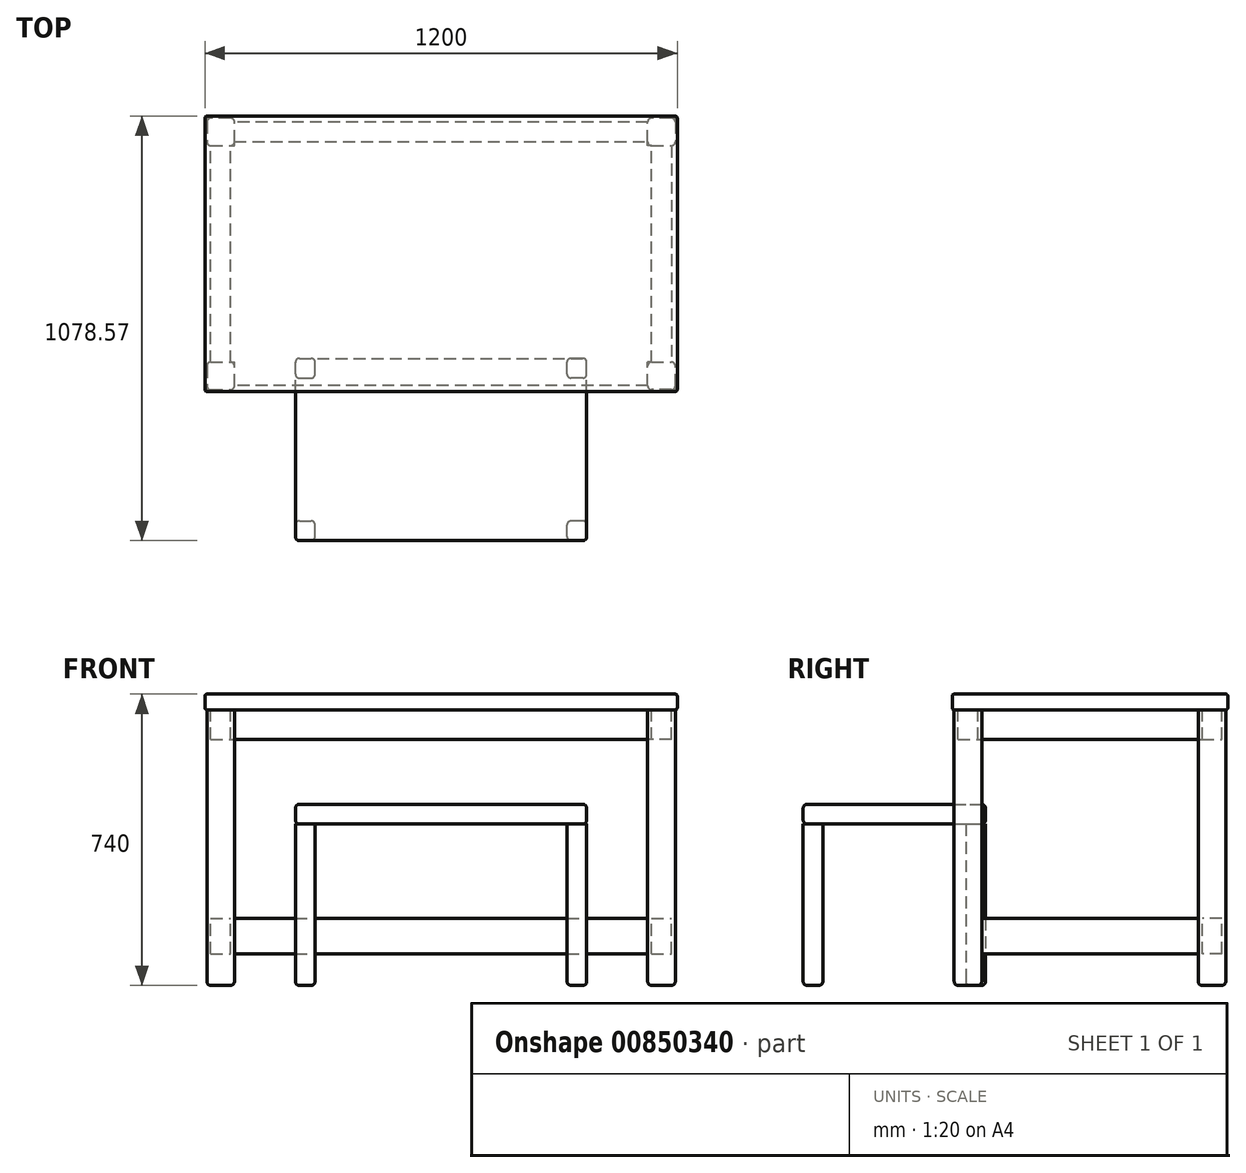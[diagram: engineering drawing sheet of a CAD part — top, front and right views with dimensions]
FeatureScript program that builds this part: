
annotation { "Feature Type Name" : "Feature", "Feature Type Description" : "" }
export const myFeature = defineFeature(function(context is Context, id is Id, definition is map)
    precondition{}
    {
        {
            var Q0;
            Q0=qCreatedBy(makeId("Top.planeOp"),FACE);
            var sketch = newSketch(context, id + "F0", { "sketchPlane" : qUnion([Q0])});
            skLineSegment(sketch, "E0.bottom", {"start": v(60, 35) * mm, "end": v(-60, 35) * mm});
            skLineSegment(sketch, "E0.top", {"start": v(60, -35) * mm, "end": v(-60, -35) * mm});
            skLineSegment(sketch, "E0.left", {"start": v(60, 35) * mm, "end": v(60, -35) * mm});
            skLineSegment(sketch, "E0.right", {"start": v(-60, 35) * mm, "end": v(-60, -35) * mm});
            skPoint(sketch, "E0.middle", {"position": v(0, 0) * mm});
            skSolve(sketch);
        }
        {
            var Q0;
            Q0=qSketchRegion(id+"F0",true);
            extrude(context, id + "F1", {"entities" : qUnion([Q0]), "depth" : 4 * mm, "offsetDistance" : 25 * mm});
        }
        {
            var Q0;
            Q0=makeQuery(id+"F1.opExtrude","CAP_EDGE",EDGE,{"disambiguationData":[OSD([sQuery(id+"F0.wireOp",EDGE,"E0.right")])],"isStart":false});
            var Q1;
            Q1=makeQuery(id+"F1.opExtrude","CAP_EDGE",EDGE,{"disambiguationData":[OSD([sQuery(id+"F0.wireOp",EDGE,"E0.right")])],"isStart":true});
            var Q2;
            Q2=makeQuery(id+"F1.opExtrude","SWEPT_EDGE",EDGE,{"disambiguationData":[OSD([sQuery(id+"F0.wireOp",EDGE,"E0.top"),sQuery(id+"F0.wireOp",EDGE,"E0.right")])]});
            var Q3;
            Q3=makeQuery(id+"F1.opExtrude","CAP_EDGE",EDGE,{"disambiguationData":[OSD([sQuery(id+"F0.wireOp",EDGE,"E0.top")])],"isStart":true});
            var Q4;
            Q4=makeQuery(id+"F1.opExtrude","CAP_EDGE",EDGE,{"disambiguationData":[OSD([sQuery(id+"F0.wireOp",EDGE,"E0.top")])],"isStart":false});
            var Q5;
            Q5=makeQuery(id+"F1.opExtrude","SWEPT_EDGE",EDGE,{"disambiguationData":[OSD([sQuery(id+"F0.wireOp",EDGE,"E0.top"),sQuery(id+"F0.wireOp",EDGE,"E0.left")])]});
            var Q6;
            Q6=makeQuery(id+"F1.opExtrude","CAP_EDGE",EDGE,{"disambiguationData":[OSD([sQuery(id+"F0.wireOp",EDGE,"E0.left")])],"isStart":true});
            var Q7;
            Q7=makeQuery(id+"F1.opExtrude","CAP_EDGE",EDGE,{"disambiguationData":[OSD([sQuery(id+"F0.wireOp",EDGE,"E0.left")])],"isStart":false});
            var Q8;
            Q8=makeQuery(id+"F1.opExtrude","SWEPT_EDGE",EDGE,{"disambiguationData":[OSD([sQuery(id+"F0.wireOp",EDGE,"E0.bottom"),sQuery(id+"F0.wireOp",EDGE,"E0.left")])]});
            var Q9;
            Q9=makeQuery(id+"F1.opExtrude","CAP_EDGE",EDGE,{"disambiguationData":[OSD([sQuery(id+"F0.wireOp",EDGE,"E0.bottom")])],"isStart":false});
            var Q10;
            Q10=makeQuery(id+"F1.opExtrude","CAP_EDGE",EDGE,{"disambiguationData":[OSD([sQuery(id+"F0.wireOp",EDGE,"E0.bottom")])],"isStart":true});
            var Q11;
            Q11=makeQuery(id+"F1.opExtrude","SWEPT_EDGE",EDGE,{"disambiguationData":[OSD([sQuery(id+"F0.wireOp",EDGE,"E0.bottom"),sQuery(id+"F0.wireOp",EDGE,"E0.right")])]});
            fillet(context, id + "F2", {"entities" : qUnion([Q0, Q1, Q2, Q3, Q4, Q5, Q6, Q7, Q8, Q9, Q10, Q11]), "radius" : 0.5 * mm, "tangentPropagation" : true, "allowEdgeOverflow" : false});
        }
        {
            var Q0;
            Q0=qCreatedBy(makeId("Top.planeOp"),FACE);
            var sketch = newSketch(context, id + "F3", { "sketchPlane" : qUnion([Q0])});
            skLineSegment(sketch, "E1.bottom", {"start": v(-59.5, -34.5) * mm, "end": v(-52.5, -34.5) * mm});
            skLineSegment(sketch, "E1.top", {"start": v(-59.5, -27.5) * mm, "end": v(-52.5, -27.5) * mm});
            skLineSegment(sketch, "E1.left", {"start": v(-59.5, -34.5) * mm, "end": v(-59.5, -27.5) * mm});
            skLineSegment(sketch, "E1.right", {"start": v(-52.5, -34.5) * mm, "end": v(-52.5, -27.5) * mm});
            skLineSegment(sketch, "E2.bottom", {"start": v(59.5, -34.5) * mm, "end": v(52.5, -34.5) * mm});
            skLineSegment(sketch, "E2.top", {"start": v(59.5, -27.5) * mm, "end": v(52.5, -27.5) * mm});
            skLineSegment(sketch, "E2.left", {"start": v(59.5, -34.5) * mm, "end": v(59.5, -27.5) * mm});
            skLineSegment(sketch, "E2.right", {"start": v(52.5, -34.5) * mm, "end": v(52.5, -27.5) * mm});
            skLineSegment(sketch, "E3.bottom", {"start": v(59.5, 34.5) * mm, "end": v(52.5, 34.5) * mm});
            skLineSegment(sketch, "E3.top", {"start": v(59.5, 27.5) * mm, "end": v(52.5, 27.5) * mm});
            skLineSegment(sketch, "E3.left", {"start": v(59.5, 34.5) * mm, "end": v(59.5, 27.5) * mm});
            skLineSegment(sketch, "E3.right", {"start": v(52.5, 34.5) * mm, "end": v(52.5, 27.5) * mm});
            skLineSegment(sketch, "E4.bottom", {"start": v(-59.5, 34.5) * mm, "end": v(-52.5, 34.5) * mm});
            skLineSegment(sketch, "E4.top", {"start": v(-59.5, 27.5) * mm, "end": v(-52.5, 27.5) * mm});
            skLineSegment(sketch, "E4.left", {"start": v(-59.5, 34.5) * mm, "end": v(-59.5, 27.5) * mm});
            skLineSegment(sketch, "E4.right", {"start": v(-52.5, 34.5) * mm, "end": v(-52.5, 27.5) * mm});
            skSolve(sketch);
        }
        {
            var Q0;
            Q0=qSketchRegion(id+"F3",true);
            extrude(context, id + "F4", {"entities" : qUnion([Q0]), "operationType" : NewBodyOperationType.ADD, "oppositeDirection" : true, "depth" : 70 * mm, "offsetDistance" : 25 * mm});
        }
        {
            var Q0;
            Q0=makeQuery(id+"F4.opExtrude","SWEPT_EDGE",EDGE,{"disambiguationData":[OSD([sQuery(id+"F3.wireOp",EDGE,"E1.bottom"),sQuery(id+"F3.wireOp",EDGE,"E1.left")])]});
            var Q1;
            Q1=makeQuery(id+"F4.opExtrude","SWEPT_EDGE",EDGE,{"disambiguationData":[OSD([sQuery(id+"F3.wireOp",EDGE,"E1.bottom"),sQuery(id+"F3.wireOp",EDGE,"E1.right")])]});
            var Q2;
            Q2=makeQuery(id+"F4.opExtrude","SWEPT_EDGE",EDGE,{"disambiguationData":[OSD([sQuery(id+"F3.wireOp",EDGE,"E1.top"),sQuery(id+"F3.wireOp",EDGE,"E1.left")])]});
            var Q3;
            Q3=makeQuery(id+"F4.opExtrude","SWEPT_EDGE",EDGE,{"disambiguationData":[OSD([sQuery(id+"F3.wireOp",EDGE,"E1.top"),sQuery(id+"F3.wireOp",EDGE,"E1.right")])]});
            var Q4;
            Q4=makeQuery(id+"F4.opExtrude","CAP_EDGE",EDGE,{"disambiguationData":[OSD([sQuery(id+"F3.wireOp",EDGE,"E1.left")])],"isStart":false});
            var Q5;
            Q5=makeQuery(id+"F4.opExtrude","CAP_EDGE",EDGE,{"disambiguationData":[OSD([sQuery(id+"F3.wireOp",EDGE,"E1.top")])],"isStart":false});
            var Q6;
            Q6=makeQuery(id+"F4.opExtrude","CAP_EDGE",EDGE,{"disambiguationData":[OSD([sQuery(id+"F3.wireOp",EDGE,"E1.right")])],"isStart":false});
            var Q7;
            Q7=makeQuery(id+"F4.opExtrude","CAP_EDGE",EDGE,{"disambiguationData":[OSD([sQuery(id+"F3.wireOp",EDGE,"E1.bottom")])],"isStart":false});
            var Q8;
            Q8=makeQuery(id+"F4.opExtrude","SWEPT_EDGE",EDGE,{"disambiguationData":[OSD([sQuery(id+"F3.wireOp",EDGE,"E2.bottom"),sQuery(id+"F3.wireOp",EDGE,"E2.left")])]});
            var Q9;
            Q9=makeQuery(id+"F4.opExtrude","SWEPT_EDGE",EDGE,{"disambiguationData":[OSD([sQuery(id+"F3.wireOp",EDGE,"E2.top"),sQuery(id+"F3.wireOp",EDGE,"E2.left")])]});
            var Q10;
            Q10=makeQuery(id+"F4.opExtrude","SWEPT_EDGE",EDGE,{"disambiguationData":[OSD([sQuery(id+"F3.wireOp",EDGE,"E2.bottom"),sQuery(id+"F3.wireOp",EDGE,"E2.right")])]});
            var Q11;
            Q11=makeQuery(id+"F4.opExtrude","SWEPT_EDGE",EDGE,{"disambiguationData":[OSD([sQuery(id+"F3.wireOp",EDGE,"E2.top"),sQuery(id+"F3.wireOp",EDGE,"E2.right")])]});
            var Q12;
            Q12=makeQuery(id+"F4.opExtrude","CAP_EDGE",EDGE,{"disambiguationData":[OSD([sQuery(id+"F3.wireOp",EDGE,"E2.bottom")])],"isStart":false});
            var Q13;
            Q13=makeQuery(id+"F4.opExtrude","CAP_EDGE",EDGE,{"disambiguationData":[OSD([sQuery(id+"F3.wireOp",EDGE,"E2.left")])],"isStart":false});
            var Q14;
            Q14=makeQuery(id+"F4.opExtrude","CAP_EDGE",EDGE,{"disambiguationData":[OSD([sQuery(id+"F3.wireOp",EDGE,"E2.top")])],"isStart":false});
            var Q15;
            Q15=makeQuery(id+"F4.opExtrude","CAP_EDGE",EDGE,{"disambiguationData":[OSD([sQuery(id+"F3.wireOp",EDGE,"E2.right")])],"isStart":false});
            var Q16;
            Q16=makeQuery(id+"F4.opExtrude","SWEPT_EDGE",EDGE,{"disambiguationData":[OSD([sQuery(id+"F3.wireOp",EDGE,"E3.bottom"),sQuery(id+"F3.wireOp",EDGE,"E3.left")])]});
            var Q17;
            Q17=makeQuery(id+"F4.opExtrude","SWEPT_EDGE",EDGE,{"disambiguationData":[OSD([sQuery(id+"F3.wireOp",EDGE,"E3.top"),sQuery(id+"F3.wireOp",EDGE,"E3.left")])]});
            var Q18;
            Q18=makeQuery(id+"F4.opExtrude","SWEPT_EDGE",EDGE,{"disambiguationData":[OSD([sQuery(id+"F3.wireOp",EDGE,"E3.bottom"),sQuery(id+"F3.wireOp",EDGE,"E3.right")])]});
            var Q19;
            Q19=makeQuery(id+"F4.opExtrude","SWEPT_EDGE",EDGE,{"disambiguationData":[OSD([sQuery(id+"F3.wireOp",EDGE,"E3.top"),sQuery(id+"F3.wireOp",EDGE,"E3.right")])]});
            var Q20;
            Q20=makeQuery(id+"F4.opExtrude","CAP_EDGE",EDGE,{"disambiguationData":[OSD([sQuery(id+"F3.wireOp",EDGE,"E3.top")])],"isStart":false});
            var Q21;
            Q21=makeQuery(id+"F4.opExtrude","CAP_EDGE",EDGE,{"disambiguationData":[OSD([sQuery(id+"F3.wireOp",EDGE,"E3.left")])],"isStart":false});
            var Q22;
            Q22=makeQuery(id+"F4.opExtrude","CAP_EDGE",EDGE,{"disambiguationData":[OSD([sQuery(id+"F3.wireOp",EDGE,"E3.bottom")])],"isStart":false});
            var Q23;
            Q23=makeQuery(id+"F4.opExtrude","CAP_EDGE",EDGE,{"disambiguationData":[OSD([sQuery(id+"F3.wireOp",EDGE,"E3.right")])],"isStart":false});
            var Q24;
            Q24=makeQuery(id+"F4.opExtrude","SWEPT_EDGE",EDGE,{"disambiguationData":[OSD([sQuery(id+"F3.wireOp",EDGE,"E4.top"),sQuery(id+"F3.wireOp",EDGE,"E4.left")])]});
            var Q25;
            Q25=makeQuery(id+"F4.opExtrude","SWEPT_EDGE",EDGE,{"disambiguationData":[OSD([sQuery(id+"F3.wireOp",EDGE,"E4.top"),sQuery(id+"F3.wireOp",EDGE,"E4.right")])]});
            var Q26;
            Q26=makeQuery(id+"F4.opExtrude","SWEPT_EDGE",EDGE,{"disambiguationData":[OSD([sQuery(id+"F3.wireOp",EDGE,"E4.bottom"),sQuery(id+"F3.wireOp",EDGE,"E4.left")])]});
            var Q27;
            Q27=makeQuery(id+"F4.opExtrude","SWEPT_EDGE",EDGE,{"disambiguationData":[OSD([sQuery(id+"F3.wireOp",EDGE,"E4.bottom"),sQuery(id+"F3.wireOp",EDGE,"E4.right")])]});
            var Q28;
            Q28=makeQuery(id+"F4.opExtrude","CAP_EDGE",EDGE,{"disambiguationData":[OSD([sQuery(id+"F3.wireOp",EDGE,"E4.right")])],"isStart":false});
            var Q29;
            Q29=makeQuery(id+"F4.opExtrude","CAP_EDGE",EDGE,{"disambiguationData":[OSD([sQuery(id+"F3.wireOp",EDGE,"E4.top")])],"isStart":false});
            var Q30;
            Q30=makeQuery(id+"F4.opExtrude","CAP_EDGE",EDGE,{"disambiguationData":[OSD([sQuery(id+"F3.wireOp",EDGE,"E4.bottom")])],"isStart":false});
            var Q31;
            Q31=makeQuery(id+"F4.opExtrude","CAP_EDGE",EDGE,{"disambiguationData":[OSD([sQuery(id+"F3.wireOp",EDGE,"E4.left")])],"isStart":false});
            fillet(context, id + "F5", {"entities" : qUnion([Q0, Q1, Q2, Q3, Q4, Q5, Q6, Q7, Q8, Q9, Q10, Q11, Q12, Q13, Q14, Q15, Q16, Q17, Q18, Q19, Q20, Q21, Q22, Q23, Q24, Q25, Q26, Q27, Q28, Q29, Q30, Q31]), "radius" : 1 * mm, "tangentPropagation" : true, "allowEdgeOverflow" : false});
        }
        {
            var Q0;
            Q0=makeQuery(id+"F4.opExtrude","SWEPT_FACE",FACE,{"disambiguationData":[OSD([sQuery(id+"F3.wireOp",EDGE,"E3.top")])]});
            var sketch = newSketch(context, id + "F6", { "sketchPlane" : qUnion([Q0])});
            skLineSegment(sketch, "E5.bottom", {"start": v(53.5, -62) * mm, "end": v(58.5, -62) * mm});
            skLineSegment(sketch, "E5.top", {"start": v(53.5, -53) * mm, "end": v(58.5, -53) * mm});
            skLineSegment(sketch, "E5.left", {"start": v(53.5, -62) * mm, "end": v(53.5, -53) * mm});
            skLineSegment(sketch, "E5.right", {"start": v(58.5, -62) * mm, "end": v(58.5, -53) * mm});
            skSolve(sketch);
        }
        {
            var Q0;
            Q0=qSketchRegion(id+"F6",true);
            extrude(context, id + "F7", {"entities" : qUnion([Q0]), "operationType" : NewBodyOperationType.ADD, "depth" : 55 * mm, "offsetDistance" : 25 * mm});
        }
        {
            var Q0;
            Q0=makeQuery(id+"F4.opExtrude","SWEPT_FACE",FACE,{"disambiguationData":[OSD([sQuery(id+"F3.wireOp",EDGE,"E4.top")])]});
            var sketch = newSketch(context, id + "F8", { "sketchPlane" : qUnion([Q0])});
            skLineSegment(sketch, "E6.bottom", {"start": v(-58.5, -62) * mm, "end": v(-53.5, -62) * mm});
            skLineSegment(sketch, "E6.top", {"start": v(-58.5, -53) * mm, "end": v(-53.5, -53) * mm});
            skLineSegment(sketch, "E6.left", {"start": v(-58.5, -62) * mm, "end": v(-58.5, -53) * mm});
            skLineSegment(sketch, "E6.right", {"start": v(-53.5, -62) * mm, "end": v(-53.5, -53) * mm});
            skSolve(sketch);
        }
        {
            var Q0;
            Q0=qSketchRegion(id+"F8",true);
            extrude(context, id + "F9", {"entities" : qUnion([Q0]), "operationType" : NewBodyOperationType.ADD, "depth" : 55 * mm, "offsetDistance" : 25 * mm});
        }
        {
            var Q0;
            Q0=makeQuery(id+"F4.opExtrude","SWEPT_FACE",FACE,{"disambiguationData":[OSD([sQuery(id+"F3.wireOp",EDGE,"E3.right")])]});
            var sketch = newSketch(context, id + "F10", { "sketchPlane" : qUnion([Q0])});
            skLineSegment(sketch, "E7.bottom", {"start": v(-33.5, -62) * mm, "end": v(-28.5, -62) * mm});
            skLineSegment(sketch, "E7.top", {"start": v(-33.5, -53) * mm, "end": v(-28.5, -53) * mm});
            skLineSegment(sketch, "E7.left", {"start": v(-33.5, -62) * mm, "end": v(-33.5, -53) * mm});
            skLineSegment(sketch, "E7.right", {"start": v(-28.5, -62) * mm, "end": v(-28.5, -53) * mm});
            skSolve(sketch);
        }
        {
            var Q0;
            Q0=qSketchRegion(id+"F10",true);
            extrude(context, id + "F11", {"entities" : qUnion([Q0]), "operationType" : NewBodyOperationType.ADD, "depth" : 105 * mm, "offsetDistance" : 25 * mm});
        }
        {
            var Q0;
            Q0=makeQuery(id+"F4.opExtrude","SWEPT_FACE",FACE,{"disambiguationData":[OSD([sQuery(id+"F3.wireOp",EDGE,"E1.right")])]});
            var sketch = newSketch(context, id + "F12", { "sketchPlane" : qUnion([Q0])});
            skLineSegment(sketch, "E8.bottom", {"start": v(-33.5, -7.5) * mm, "end": v(33.5, -7.5) * mm});
            skLineSegment(sketch, "E8.top", {"start": v(-33.5, 0) * mm, "end": v(33.5, 0) * mm});
            skLineSegment(sketch, "E8.left", {"start": v(-33.5, -7.5) * mm, "end": v(-33.5, 0) * mm});
            skLineSegment(sketch, "E8.right", {"start": v(33.5, -7.5) * mm, "end": v(33.5, 0) * mm});
            skSolve(sketch);
        }
        {
            var Q0;
            Q0=qSketchRegion(id+"F12",true);
            extrude(context, id + "F13", {"entities" : qUnion([Q0]), "operationType" : NewBodyOperationType.ADD, "depth" : 105 * mm, "offsetDistance" : 25 * mm});
        }
        {
            var Q0;
            {var subQ1=sQuery(id+"F3.wireOp",EDGE,"E2.top");Q0=makeQuery(id+"F7.boolean.opBoolean","SPLIT",FACE,{"disambiguationData":[TD([makeQuery(id+"F7.opExtrude","SWEPT_FACE",FACE,{"disambiguationData":[OSD([sQuery(id+"F6.wireOp",EDGE,"E5.top")])]})])],"derivedFrom":makeQuery(id+"F4.opExtrude","SWEPT_FACE",FACE,{"disambiguationData":[OSD([subQ1])]})});}
            var sketch = newSketch(context, id + "F14", { "sketchPlane" : qUnion([Q0])});
            skLineSegment(sketch, "E9.bottom", {"start": v(-58.5, -7.5) * mm, "end": v(-52.5, -7.5) * mm});
            skLineSegment(sketch, "E9.top", {"start": v(-58.5, 0) * mm, "end": v(-52.5, 0) * mm});
            skLineSegment(sketch, "E9.left", {"start": v(-58.5, -7.5) * mm, "end": v(-58.5, 0) * mm});
            skLineSegment(sketch, "E9.right", {"start": v(-52.5, -7.5) * mm, "end": v(-52.5, 0) * mm});
            skSolve(sketch);
        }
        {
            var Q0;
            Q0=qSketchRegion(id+"F14",true);
            extrude(context, id + "F15", {"entities" : qUnion([Q0]), "operationType" : NewBodyOperationType.ADD, "depth" : 55 * mm, "offsetDistance" : 25 * mm});
        }
        {
            var Q0;
            {var subQ1=sQuery(id+"F3.wireOp",EDGE,"E4.top");Q0=makeQuery(id+"F9.boolean.opBoolean","SPLIT",FACE,{"disambiguationData":[TD([makeQuery(id+"F9.opExtrude","SWEPT_FACE",FACE,{"disambiguationData":[OSD([sQuery(id+"F8.wireOp",EDGE,"E6.top")])]})])],"derivedFrom":makeQuery(id+"F4.opExtrude","SWEPT_FACE",FACE,{"disambiguationData":[OSD([subQ1])]})});}
            var sketch = newSketch(context, id + "F16", { "sketchPlane" : qUnion([Q0])});
            skLineSegment(sketch, "E10.bottom", {"start": v(-58.5, -7.5) * mm, "end": v(-52.5, -7.5) * mm});
            skLineSegment(sketch, "E10.top", {"start": v(-58.5, 0) * mm, "end": v(-52.5, 0) * mm});
            skLineSegment(sketch, "E10.left", {"start": v(-58.5, -7.5) * mm, "end": v(-58.5, 0) * mm});
            skLineSegment(sketch, "E10.right", {"start": v(-52.5, -7.5) * mm, "end": v(-52.5, 0) * mm});
            skSolve(sketch);
        }
        {
            var Q0;
            Q0=qSketchRegion(id+"F16",true);
            extrude(context, id + "F17", {"entities" : qUnion([Q0]), "operationType" : NewBodyOperationType.ADD, "depth" : 55 * mm, "offsetDistance" : 25 * mm});
        }
        {
            var Q0;
            Q0=makeQuery(id+"F1.opExtrude","SWEPT_BODY",BODY,{"disambiguationData":[OSD([sQuery(id+"F0.wireOp",EDGE,"E0.bottom"),sQuery(id+"F0.wireOp",EDGE,"E0.top"),sQuery(id+"F0.wireOp",EDGE,"E0.left"),sQuery(id+"F0.wireOp",EDGE,"E0.right")])]});
            var Q1;
            Q1=qCreatedBy(makeId("Origin.pointOp"),VERTEX);
            transform(context, id + "F18", {"entities" : qUnion([Q0]), "transformType" : TransformType.SCALE_UNIFORMLY, "scale" : 10, "scalePoint" : qUnion([Q1]), "makeCopy" : false});
        }
        {
            var Q0;
            Q0=makeQuery(id+"F4.opExtrude","CAP_FACE",FACE,{"disambiguationData":[OSD([sQuery(id+"F3.wireOp",EDGE,"E1.bottom"),sQuery(id+"F3.wireOp",EDGE,"E1.top"),sQuery(id+"F3.wireOp",EDGE,"E1.left"),sQuery(id+"F3.wireOp",EDGE,"E1.right")])],"isStart":false});
            var sketch = newSketch(context, id + "F19", { "sketchPlane" : qUnion([Q0])});
            skLineSegment(sketch, "E11.bottom", {"start": v(-370.07, 315.43) * mm, "end": v(-320.07, 315.43) * mm});
            skLineSegment(sketch, "E11.top", {"start": v(-370.07, 265.43) * mm, "end": v(-320.07, 265.43) * mm});
            skLineSegment(sketch, "E11.left", {"start": v(-370.07, 315.43) * mm, "end": v(-370.07, 265.43) * mm});
            skLineSegment(sketch, "E11.right", {"start": v(-320.07, 315.43) * mm, "end": v(-320.07, 265.43) * mm});
            skSolve(sketch);
        }
        {
            var Q0;
            Q0=qSketchRegion(id+"F19",true);
            extrude(context, id + "F20", {"entities" : qUnion([Q0]), "oppositeDirection" : true, "depth" : 410 * mm, "offsetDistance" : 25 * mm});
        }
        {
            var Q0;
            Q0=makeQuery(id+"F20.opExtrude","SWEPT_BODY",BODY,{"disambiguationData":[OSD([sQuery(id+"F19.wireOp",EDGE,"E11.bottom"),sQuery(id+"F19.wireOp",EDGE,"E11.top"),sQuery(id+"F19.wireOp",EDGE,"E11.left"),sQuery(id+"F19.wireOp",EDGE,"E11.right")])]});
            var Q1;
            Q1=qCreatedBy(makeId("Right.planeOp"),FACE);
            mirror(context, id + "F21", {"entities" : qUnion([Q0]), "mirrorPlane" : qUnion([Q1])});
        }
        {
            var Q0;
            Q0=makeQuery(id+"F20.opExtrude","CAP_FACE",FACE,{"disambiguationData":[OSD([sQuery(id+"F19.wireOp",EDGE,"E11.bottom"),sQuery(id+"F19.wireOp",EDGE,"E11.top"),sQuery(id+"F19.wireOp",EDGE,"E11.left"),sQuery(id+"F19.wireOp",EDGE,"E11.right")])],"isStart":true});
            var sketch = newSketch(context, id + "F22", { "sketchPlane" : qUnion([Q0])});
            skLineSegment(sketch, "E12.bottom", {"start": v(-370.07, 528.57) * mm, "end": v(-320.07, 528.57) * mm});
            skLineSegment(sketch, "E12.top", {"start": v(-370.07, 478.57) * mm, "end": v(-320.07, 478.57) * mm});
            skLineSegment(sketch, "E12.left", {"start": v(-370.07, 528.57) * mm, "end": v(-370.07, 478.57) * mm});
            skLineSegment(sketch, "E12.right", {"start": v(-320.07, 528.57) * mm, "end": v(-320.07, 478.57) * mm});
            skSolve(sketch);
        }
        {
            var Q0;
            Q0=qSketchRegion(id+"F22",true);
            extrude(context, id + "F23", {"entities" : qUnion([Q0]), "oppositeDirection" : true, "depth" : 410 * mm, "offsetDistance" : 25 * mm});
        }
        {
            var Q0;
            Q0=makeQuery(id+"F23.opExtrude","SWEPT_BODY",BODY,{"disambiguationData":[OSD([sQuery(id+"F22.wireOp",EDGE,"E12.bottom"),sQuery(id+"F22.wireOp",EDGE,"E12.top"),sQuery(id+"F22.wireOp",EDGE,"E12.left"),sQuery(id+"F22.wireOp",EDGE,"E12.right")])]});
            transform(context, id + "F24", {"entities" : qUnion([Q0]), "transformType" : TransformType.TRANSLATION_3D, "dx" : 0 * mm, "dy" : -200 * mm, "dz" : 0 * mm, "makeCopy" : false});
        }
        {
            var Q0;
            Q0=makeQuery(id+"F23.opExtrude","SWEPT_BODY",BODY,{"disambiguationData":[OSD([sQuery(id+"F22.wireOp",EDGE,"E12.bottom"),sQuery(id+"F22.wireOp",EDGE,"E12.top"),sQuery(id+"F22.wireOp",EDGE,"E12.left"),sQuery(id+"F22.wireOp",EDGE,"E12.right")])]});
            var Q1;
            Q1=qCreatedBy(makeId("Right.planeOp"),FACE);
            mirror(context, id + "F25", {"entities" : qUnion([Q0]), "mirrorPlane" : qUnion([Q1])});
        }
        {
            var Q0;
            Q0=makeQuery(id+"F23.opExtrude","CAP_FACE",FACE,{"disambiguationData":[OSD([sQuery(id+"F22.wireOp",EDGE,"E12.bottom"),sQuery(id+"F22.wireOp",EDGE,"E12.top"),sQuery(id+"F22.wireOp",EDGE,"E12.left"),sQuery(id+"F22.wireOp",EDGE,"E12.right")])],"isStart":false});
            var sketch = newSketch(context, id + "F26", { "sketchPlane" : qUnion([Q0])});
            skLineSegment(sketch, "E13.bottom", {"start": v(-370.07, -728.57) * mm, "end": v(370.04, -728.57) * mm});
            skLineSegment(sketch, "E13.top", {"start": v(-370.07, -265.45) * mm, "end": v(370.04, -265.45) * mm});
            skLineSegment(sketch, "E13.left", {"start": v(-370.07, -728.57) * mm, "end": v(-370.07, -265.45) * mm});
            skLineSegment(sketch, "E13.right", {"start": v(370.04, -728.57) * mm, "end": v(370.04, -265.45) * mm});
            skSolve(sketch);
        }
        {
            var Q0;
            Q0=qSketchRegion(id+"F26",true);
            extrude(context, id + "F27", {"entities" : qUnion([Q0]), "depth" : 50 * mm, "offsetDistance" : 25 * mm});
        }
        {
            var Q0;
            Q0=makeQuery(id+"F23.opExtrude","SWEPT_EDGE",EDGE,{"disambiguationData":[OSD([sQuery(id+"F22.wireOp",EDGE,"E12.bottom"),sQuery(id+"F22.wireOp",EDGE,"E12.left")])]});
            var Q1;
            Q1=makeQuery(id+"F23.opExtrude","SWEPT_EDGE",EDGE,{"disambiguationData":[OSD([sQuery(id+"F22.wireOp",EDGE,"E12.bottom"),sQuery(id+"F22.wireOp",EDGE,"E12.right")])]});
            var Q2;
            Q2=makeQuery(id+"F23.opExtrude","SWEPT_EDGE",EDGE,{"disambiguationData":[OSD([sQuery(id+"F22.wireOp",EDGE,"E12.top"),sQuery(id+"F22.wireOp",EDGE,"E12.right")])]});
            var Q3;
            Q3=makeQuery(id+"F23.opExtrude","SWEPT_EDGE",EDGE,{"disambiguationData":[OSD([sQuery(id+"F22.wireOp",EDGE,"E12.top"),sQuery(id+"F22.wireOp",EDGE,"E12.left")])]});
            var Q4;
            Q4=makeQuery(id+"F20.opExtrude","SWEPT_EDGE",EDGE,{"disambiguationData":[OSD([sQuery(id+"F19.wireOp",EDGE,"E11.top"),sQuery(id+"F19.wireOp",EDGE,"E11.left")])]});
            var Q5;
            Q5=makeQuery(id+"F20.opExtrude","SWEPT_EDGE",EDGE,{"disambiguationData":[OSD([sQuery(id+"F19.wireOp",EDGE,"E11.top"),sQuery(id+"F19.wireOp",EDGE,"E11.right")])]});
            var Q6;
            Q6=makeQuery(id+"F20.opExtrude","SWEPT_EDGE",EDGE,{"disambiguationData":[OSD([sQuery(id+"F19.wireOp",EDGE,"E11.bottom"),sQuery(id+"F19.wireOp",EDGE,"E11.left")])]});
            var Q7;
            Q7=makeQuery(id+"F20.opExtrude","SWEPT_EDGE",EDGE,{"disambiguationData":[OSD([sQuery(id+"F19.wireOp",EDGE,"E11.bottom"),sQuery(id+"F19.wireOp",EDGE,"E11.right")])]});
            var Q8;
            Q8=makeQuery(id+"F25.opPattern","COPY",EDGE,{"derivedFrom":makeQuery(id+"F23.opExtrude","SWEPT_EDGE",EDGE,{"disambiguationData":[OSD([sQuery(id+"F22.wireOp",EDGE,"E12.bottom"),sQuery(id+"F22.wireOp",EDGE,"E12.left")])]}),"instanceName":"1"});
            var Q9;
            Q9=makeQuery(id+"F25.opPattern","COPY",EDGE,{"derivedFrom":makeQuery(id+"F23.opExtrude","SWEPT_EDGE",EDGE,{"disambiguationData":[OSD([sQuery(id+"F22.wireOp",EDGE,"E12.top"),sQuery(id+"F22.wireOp",EDGE,"E12.left")])]}),"instanceName":"1"});
            var Q10;
            Q10=makeQuery(id+"F25.opPattern","COPY",EDGE,{"derivedFrom":makeQuery(id+"F23.opExtrude","SWEPT_EDGE",EDGE,{"disambiguationData":[OSD([sQuery(id+"F22.wireOp",EDGE,"E12.bottom"),sQuery(id+"F22.wireOp",EDGE,"E12.right")])]}),"instanceName":"1"});
            var Q11;
            Q11=makeQuery(id+"F25.opPattern","COPY",EDGE,{"derivedFrom":makeQuery(id+"F23.opExtrude","SWEPT_EDGE",EDGE,{"disambiguationData":[OSD([sQuery(id+"F22.wireOp",EDGE,"E12.top"),sQuery(id+"F22.wireOp",EDGE,"E12.right")])]}),"instanceName":"1"});
            var Q12;
            Q12=makeQuery(id+"F21.opPattern","COPY",EDGE,{"derivedFrom":makeQuery(id+"F20.opExtrude","SWEPT_EDGE",EDGE,{"disambiguationData":[OSD([sQuery(id+"F19.wireOp",EDGE,"E11.bottom"),sQuery(id+"F19.wireOp",EDGE,"E11.right")])]}),"instanceName":"1"});
            var Q13;
            Q13=makeQuery(id+"F21.opPattern","COPY",EDGE,{"derivedFrom":makeQuery(id+"F20.opExtrude","SWEPT_EDGE",EDGE,{"disambiguationData":[OSD([sQuery(id+"F19.wireOp",EDGE,"E11.bottom"),sQuery(id+"F19.wireOp",EDGE,"E11.left")])]}),"instanceName":"1"});
            var Q14;
            Q14=makeQuery(id+"F21.opPattern","COPY",EDGE,{"derivedFrom":makeQuery(id+"F20.opExtrude","SWEPT_EDGE",EDGE,{"disambiguationData":[OSD([sQuery(id+"F19.wireOp",EDGE,"E11.top"),sQuery(id+"F19.wireOp",EDGE,"E11.right")])]}),"instanceName":"1"});
            var Q15;
            Q15=makeQuery(id+"F21.opPattern","COPY",EDGE,{"derivedFrom":makeQuery(id+"F20.opExtrude","SWEPT_EDGE",EDGE,{"disambiguationData":[OSD([sQuery(id+"F19.wireOp",EDGE,"E11.top"),sQuery(id+"F19.wireOp",EDGE,"E11.left")])]}),"instanceName":"1"});
            var Q16;
            Q16=makeQuery(id+"F21.opPattern","COPY",EDGE,{"derivedFrom":makeQuery(id+"F20.opExtrude","CAP_EDGE",EDGE,{"disambiguationData":[OSD([sQuery(id+"F19.wireOp",EDGE,"E11.left")])],"isStart":true}),"instanceName":"1"});
            var Q17;
            Q17=makeQuery(id+"F21.opPattern","COPY",EDGE,{"derivedFrom":makeQuery(id+"F20.opExtrude","CAP_EDGE",EDGE,{"disambiguationData":[OSD([sQuery(id+"F19.wireOp",EDGE,"E11.top")])],"isStart":true}),"instanceName":"1"});
            var Q18;
            Q18=makeQuery(id+"F21.opPattern","COPY",EDGE,{"derivedFrom":makeQuery(id+"F20.opExtrude","CAP_EDGE",EDGE,{"disambiguationData":[OSD([sQuery(id+"F19.wireOp",EDGE,"E11.right")])],"isStart":true}),"instanceName":"1"});
            var Q19;
            Q19=makeQuery(id+"F21.opPattern","COPY",EDGE,{"derivedFrom":makeQuery(id+"F20.opExtrude","CAP_EDGE",EDGE,{"disambiguationData":[OSD([sQuery(id+"F19.wireOp",EDGE,"E11.bottom")])],"isStart":true}),"instanceName":"1"});
            var Q20;
            Q20=makeQuery(id+"F20.opExtrude","CAP_EDGE",EDGE,{"disambiguationData":[OSD([sQuery(id+"F19.wireOp",EDGE,"E11.right")])],"isStart":true});
            var Q21;
            Q21=makeQuery(id+"F20.opExtrude","CAP_EDGE",EDGE,{"disambiguationData":[OSD([sQuery(id+"F19.wireOp",EDGE,"E11.top")])],"isStart":true});
            var Q22;
            Q22=makeQuery(id+"F20.opExtrude","CAP_EDGE",EDGE,{"disambiguationData":[OSD([sQuery(id+"F19.wireOp",EDGE,"E11.bottom")])],"isStart":true});
            var Q23;
            Q23=makeQuery(id+"F20.opExtrude","CAP_EDGE",EDGE,{"disambiguationData":[OSD([sQuery(id+"F19.wireOp",EDGE,"E11.left")])],"isStart":true});
            var Q24;
            Q24=makeQuery(id+"F23.opExtrude","CAP_EDGE",EDGE,{"disambiguationData":[OSD([sQuery(id+"F22.wireOp",EDGE,"E12.bottom")])],"isStart":true});
            var Q25;
            Q25=makeQuery(id+"F23.opExtrude","CAP_EDGE",EDGE,{"disambiguationData":[OSD([sQuery(id+"F22.wireOp",EDGE,"E12.left")])],"isStart":true});
            var Q26;
            Q26=makeQuery(id+"F23.opExtrude","CAP_EDGE",EDGE,{"disambiguationData":[OSD([sQuery(id+"F22.wireOp",EDGE,"E12.top")])],"isStart":true});
            var Q27;
            Q27=makeQuery(id+"F23.opExtrude","CAP_EDGE",EDGE,{"disambiguationData":[OSD([sQuery(id+"F22.wireOp",EDGE,"E12.right")])],"isStart":true});
            var Q28;
            Q28=makeQuery(id+"F25.opPattern","COPY",EDGE,{"derivedFrom":makeQuery(id+"F23.opExtrude","CAP_EDGE",EDGE,{"disambiguationData":[OSD([sQuery(id+"F22.wireOp",EDGE,"E12.left")])],"isStart":true}),"instanceName":"1"});
            var Q29;
            Q29=makeQuery(id+"F25.opPattern","COPY",EDGE,{"derivedFrom":makeQuery(id+"F23.opExtrude","CAP_EDGE",EDGE,{"disambiguationData":[OSD([sQuery(id+"F22.wireOp",EDGE,"E12.bottom")])],"isStart":true}),"instanceName":"1"});
            var Q30;
            Q30=makeQuery(id+"F25.opPattern","COPY",EDGE,{"derivedFrom":makeQuery(id+"F23.opExtrude","CAP_EDGE",EDGE,{"disambiguationData":[OSD([sQuery(id+"F22.wireOp",EDGE,"E12.right")])],"isStart":true}),"instanceName":"1"});
            var Q31;
            Q31=makeQuery(id+"F25.opPattern","COPY",EDGE,{"derivedFrom":makeQuery(id+"F23.opExtrude","CAP_EDGE",EDGE,{"disambiguationData":[OSD([sQuery(id+"F22.wireOp",EDGE,"E12.top")])],"isStart":true}),"instanceName":"1"});
            var Q32;
            Q32=makeQuery(id+"F27.opExtrude","CAP_EDGE",EDGE,{"disambiguationData":[OSD([sQuery(id+"F26.wireOp",EDGE,"E13.bottom")])],"isStart":false});
            var Q33;
            Q33=makeQuery(id+"F27.opExtrude","CAP_EDGE",EDGE,{"disambiguationData":[OSD([sQuery(id+"F26.wireOp",EDGE,"E13.bottom")])],"isStart":true});
            var Q34;
            Q34=makeQuery(id+"F27.opExtrude","CAP_EDGE",EDGE,{"disambiguationData":[OSD([sQuery(id+"F26.wireOp",EDGE,"E13.right")])],"isStart":false});
            var Q35;
            Q35=makeQuery(id+"F27.opExtrude","CAP_EDGE",EDGE,{"disambiguationData":[OSD([sQuery(id+"F26.wireOp",EDGE,"E13.right")])],"isStart":true});
            var Q36;
            Q36=makeQuery(id+"F27.opExtrude","SWEPT_EDGE",EDGE,{"disambiguationData":[OSD([sQuery(id+"F26.wireOp",EDGE,"E13.bottom"),sQuery(id+"F26.wireOp",EDGE,"E13.right")])]});
            var Q37;
            Q37=makeQuery(id+"F27.opExtrude","CAP_EDGE",EDGE,{"disambiguationData":[OSD([sQuery(id+"F26.wireOp",EDGE,"E13.left")])],"isStart":false});
            var Q38;
            Q38=makeQuery(id+"F27.opExtrude","CAP_EDGE",EDGE,{"disambiguationData":[OSD([sQuery(id+"F26.wireOp",EDGE,"E13.left")])],"isStart":true});
            var Q39;
            Q39=makeQuery(id+"F27.opExtrude","SWEPT_EDGE",EDGE,{"disambiguationData":[OSD([sQuery(id+"F26.wireOp",EDGE,"E13.bottom"),sQuery(id+"F26.wireOp",EDGE,"E13.left")])]});
            var Q40;
            Q40=makeQuery(id+"F27.opExtrude","SWEPT_EDGE",EDGE,{"disambiguationData":[OSD([sQuery(id+"F26.wireOp",EDGE,"E13.top"),sQuery(id+"F26.wireOp",EDGE,"E13.left")])]});
            var Q41;
            Q41=makeQuery(id+"F27.opExtrude","CAP_EDGE",EDGE,{"disambiguationData":[OSD([sQuery(id+"F26.wireOp",EDGE,"E13.top")])],"isStart":false});
            var Q42;
            Q42=makeQuery(id+"F27.opExtrude","CAP_EDGE",EDGE,{"disambiguationData":[OSD([sQuery(id+"F26.wireOp",EDGE,"E13.top")])],"isStart":true});
            var Q43;
            Q43=makeQuery(id+"F27.opExtrude","SWEPT_EDGE",EDGE,{"disambiguationData":[OSD([sQuery(id+"F26.wireOp",EDGE,"E13.top"),sQuery(id+"F26.wireOp",EDGE,"E13.right")])]});
            fillet(context, id + "F28", {"entities" : qUnion([Q0, Q1, Q2, Q3, Q4, Q5, Q6, Q7, Q8, Q9, Q10, Q11, Q12, Q13, Q14, Q15, Q16, Q17, Q18, Q19, Q20, Q21, Q22, Q23, Q24, Q25, Q26, Q27, Q28, Q29, Q30, Q31, Q32, Q33, Q34, Q35, Q36, Q37, Q38, Q39, Q40, Q41, Q42, Q43]), "radius" : 10 * mm, "tangentPropagation" : true, "allowEdgeOverflow" : false});
        }
    });
